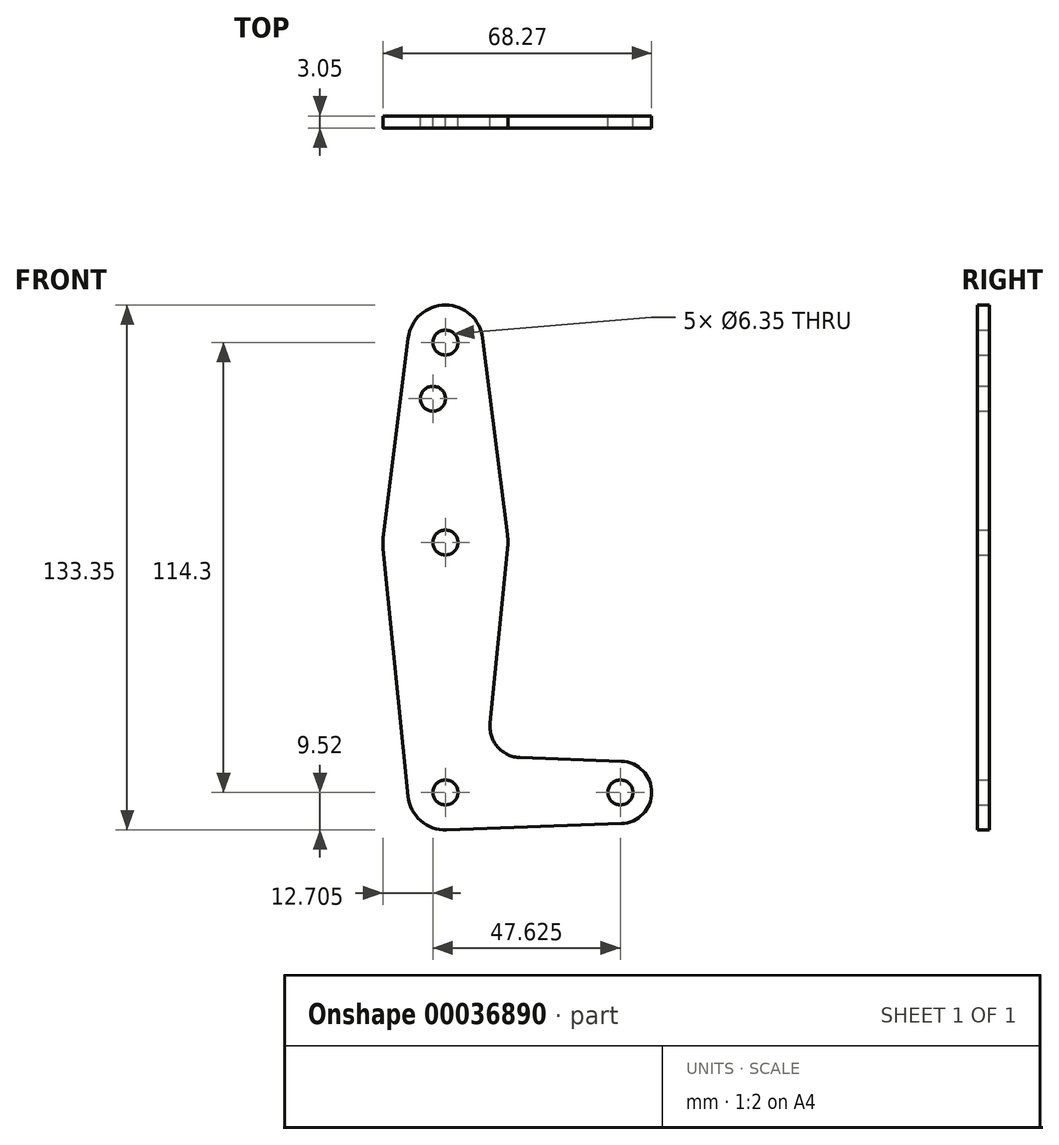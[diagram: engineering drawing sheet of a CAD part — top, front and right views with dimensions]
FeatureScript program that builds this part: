
annotation { "Feature Type Name" : "Feature", "Feature Type Description" : "" }
export const myFeature = defineFeature(function(context is Context, id is Id, definition is map)
    precondition{}
    {
        {
            var Q0;
            Q0=qCreatedBy(makeId("Front.planeOp"),FACE);
            var sketch = newSketch(context, id + "F0", { "sketchPlane" : qUnion([Q0])});
            skLineSegment(sketch, "E0", {"start": v(0, 0) * mm, "end": v(0, 63.5) * mm, "construction": true});
            skCircle(sketch, "E1", {"center": v(0, 63.5) * mm, "radius": 15.88 * mm});
            skLineSegment(sketch, "E2", {"start": v(0, 63.5) * mm, "end": v(0, 114.3) * mm, "construction": true});
            skCircle(sketch, "E3", {"center": v(0, 114.3) * mm, "radius": 9.52 * mm});
            skCircle(sketch, "E4", {"center": v(44.45, 0) * mm, "radius": 7.94 * mm});
            skLineSegment(sketch, "E5", {"start": v(0, 0) * mm, "end": v(44.45, 0) * mm, "construction": true});
            skLineSegment(sketch, "E6", {"start": v(-9.45, 115.5) * mm, "end": v(-15.75, 65.48) * mm});
            skLineSegment(sketch, "E7", {"start": v(9.45, 115.5) * mm, "end": v(15.75, 65.48) * mm});
            skCircle(sketch, "E8", {"center": v(0, 0) * mm, "radius": 9.53 * mm});
            skLineSegment(sketch, "E9", {"start": v(-15.8, 61.91) * mm, "end": v(-9.48, -0.95) * mm});
            skLineSegment(sketch, "E10", {"start": v(15.8, 61.91) * mm, "end": v(11.34, 17.6) * mm});
            skLineSegment(sketch, "E11", {"start": v(0.34, -9.52) * mm, "end": v(44.73, -7.93) * mm});
            skLineSegment(sketch, "E12", {"start": v(18.97, 8.85) * mm, "end": v(44.73, 7.93) * mm});
            skCircle(sketch, "E13", {"center": v(0, 63.5) * mm, "radius": 3.18 * mm});
            skCircle(sketch, "E14", {"center": v(0, 114.3) * mm, "radius": 3.18 * mm});
            skCircle(sketch, "E15", {"center": v(0, 0) * mm, "radius": 3.18 * mm});
            skCircle(sketch, "E16", {"center": v(44.45, 0) * mm, "radius": 3.18 * mm});
            skArc(sketch, "E17.filletArc", {"start": v(11.34, 17.6) * mm, "mid": v(13.26, 11.57) * mm, "end": v(18.97, 8.85) * mm});
            skCircle(sketch, "E18", {"center": v(-3.18, 100.03) * mm, "radius": 3.18 * mm});
            skSolve(sketch);
        }
        {
            var Q0;
            Q0=makeQuery(id+"F0.imprint","IMPRINT",FACE,{"disambiguationData":[TD([[makeQuery(id+"F0.imprint","IMPRINT",EDGE,{"derivedFrom":sQuery(id+"F0.wireOp",EDGE,"E14")}),-1.0]])]});
            var Q1;
            Q1=makeQuery(id+"F0.imprint","IMPRINT",FACE,{"disambiguationData":[TD([[makeQuery(id+"F0.imprint","IMPRINT",EDGE,{"derivedFrom":sQuery(id+"F0.wireOp",EDGE,"E16")}),-1.0]])]});
            var Q2;
            Q2=makeQuery(id+"F0.imprint","IMPRINT",FACE,{"disambiguationData":[TD([[makeQuery(id+"F0.imprint","IMPRINT",EDGE,{"derivedFrom":sQuery(id+"F0.wireOp",EDGE,"E15")}),-1.0]])]});
            var Q3;
            Q3=makeQuery(id+"F0.imprint","IMPRINT",FACE,{"disambiguationData":[TD([[makeQuery(id+"F0.imprint","IMPRINT",EDGE,{"derivedFrom":sQuery(id+"F0.wireOp",EDGE,"E13")}),-1.0]])]});
            var Q4;
            {var subQ4=sQuery(id+"F0.wireOp",EDGE,"E9");Q4=makeQuery(id+"F0.imprint","IMPRINT",FACE,{"disambiguationData":[TD([[makeQuery(id+"F0.imprint","IMPRINT",EDGE,{"derivedFrom":subQ4}),1.0]])]});}
            var Q5;
            {var subQ2=sQuery(id+"F0.wireOp",EDGE,"E6");Q5=makeQuery(id+"F0.imprint","IMPRINT",FACE,{"disambiguationData":[TD([[makeQuery(id+"F0.imprint","IMPRINT",EDGE,{"derivedFrom":subQ2}),1.0]])]});}
            extrude(context, id + "F1", {"entities" : qUnion([Q0, Q1, Q2, Q3, Q4, Q5]), "depth" : 3.05 * mm});
        }
    });
